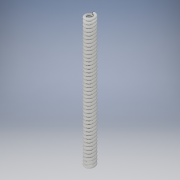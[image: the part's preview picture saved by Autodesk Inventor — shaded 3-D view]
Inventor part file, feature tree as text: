
AUTODESK INVENTOR PART (.ipt)
format: ipt  version: 2018 (Build 220112000, 112)  size: 1,011,200 bytes
history: native  units: in
note: dims shown in document units (in); Inventor stores cm internally (conversion verified against a paired STEP export)
features: helix x1, sketch x1
ambient origin geometry x8: Origin, YZ Plane, XZ Plane, XY Plane, X Axis, Y Axis, Z Axis, Center Point
bodies: Solid1 (feature_tree)
feature tree (2):
  helix  "Coil1"  [1 undecoded]
  sketch  "Sketch1"  dims[d1=0.044in d2=1.0in d3=1.1in d4=15.748in d5=0.0in d6=90.0deg d7=0.3436in d8=90.0deg d9=0.3436in]
note: 1 required parameter value undecoded (feature->parameter linkage not recoverable at this tier; creation-order binding heuristic only, values carry confidence <= 0.55)
